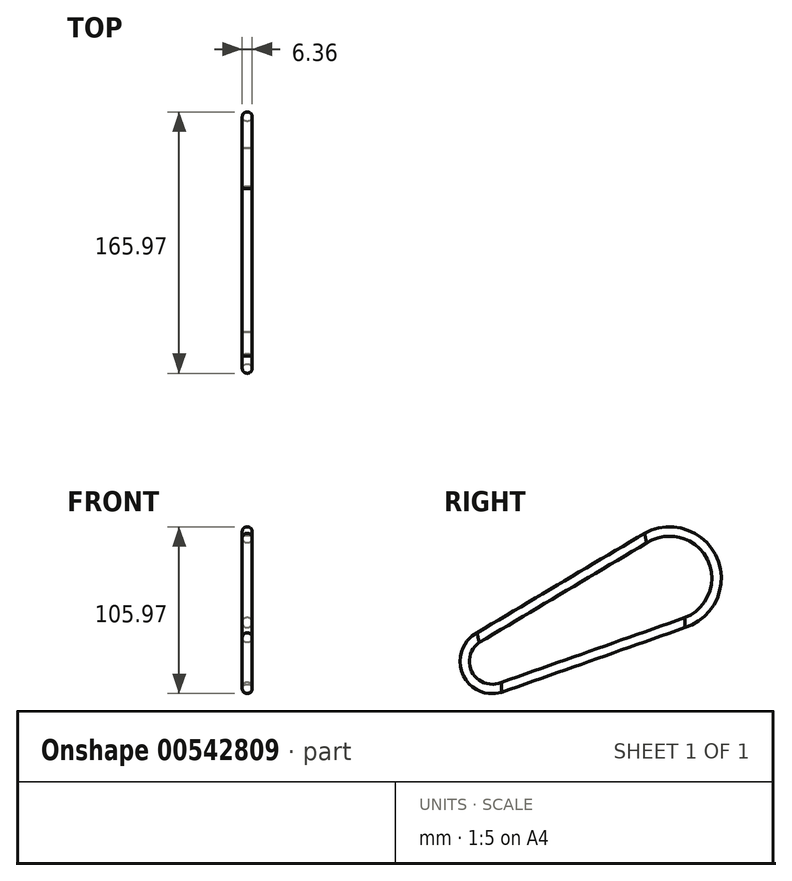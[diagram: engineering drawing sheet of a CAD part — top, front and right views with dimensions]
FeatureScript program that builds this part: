
annotation { "Feature Type Name" : "Feature", "Feature Type Description" : "" }
export const myFeature = defineFeature(function(context is Context, id is Id, definition is map)
    precondition{}
    {
        {
            var Q0;
            Q0=qCreatedBy(makeId("Right.planeOp"),FACE);
            var sketch = newSketch(context, id + "F0", { "sketchPlane" : qUnion([Q0])});
            skArc(sketch, "E0", {"start": v(-14.72, 31.48) * mm, "mid": v(-21.61, 9.08) * mm, "end": v(0, 0) * mm});
            skArc(sketch, "E1", {"start": v(116.78, 41.07) * mm, "mid": v(133.88, 81.77) * mm, "end": v(91.68, 94.76) * mm});
            skLineSegment(sketch, "E2", {"start": v(-5.8, 16.47) * mm, "end": v(46.85, 16.47) * mm, "construction": true});
            skLineSegment(sketch, "E3", {"start": v(106.76, 37.54) * mm, "end": v(106.9, 69.16) * mm, "construction": true});
            skLineSegment(sketch, "E4", {"start": v(-14.72, 31.48) * mm, "end": v(91.68, 94.76) * mm});
            skLineSegment(sketch, "E5", {"start": v(0, 0) * mm, "end": v(116.78, 41.07) * mm});
            skPoint(sketch, "E6.orphan", {"position": v(106.66, 16.47) * mm});
            skSolve(sketch);
        }
        {
            var Q0;
            Q0=qCreatedBy(makeId("Front.planeOp"),FACE);
            var sketch = newSketch(context, id + "F1", { "sketchPlane" : qUnion([Q0])});
            skCircle(sketch, "E7", {"center": v(0, 0) * mm, "radius": 3.18 * mm});
            skSolve(sketch);
        }
        {
            var Q0;
            Q0=makeQuery(id+"F1.imprint","IMPRINT",FACE,{"disambiguationData":[TD([[makeQuery(id+"F1.imprint","IMPRINT",EDGE,{"derivedFrom":sQuery(id+"F1.wireOp",EDGE,"E7")}),1.0]])]});
            var Q1;
            Q1=sQuery(id+"F0.wireOp",EDGE,"E5");
            var Q2;
            Q2=sQuery(id+"F0.wireOp",EDGE,"E1");
            var Q3;
            Q3=sQuery(id+"F0.wireOp",EDGE,"E4");
            var Q4;
            Q4=sQuery(id+"F0.wireOp",EDGE,"E0");
            sweep(context, id + "F2", {"profiles" : qUnion([Q0]), "path" : qUnion([Q1, Q2, Q3, Q4])});
        }
    });
